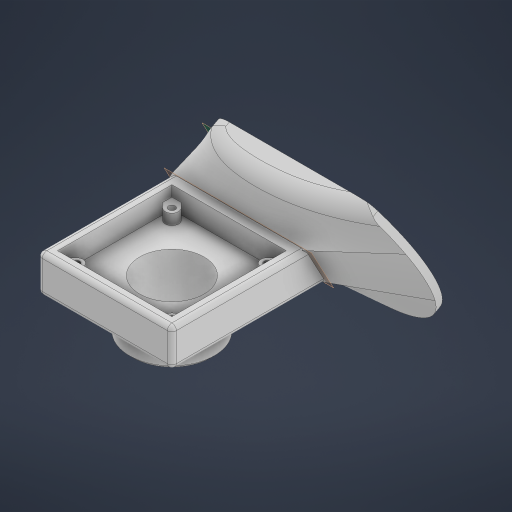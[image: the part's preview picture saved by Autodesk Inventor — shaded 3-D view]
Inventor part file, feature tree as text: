
AUTODESK INVENTOR PART (.ipt)
format: ipt  version: 2023 (Build 270158000, 158)  size: 587,264 bytes
history: native  units: in
note: dims shown in document units (in); Inventor stores cm internally (conversion verified against a paired STEP export)
features: sketch x10, extrude x7, hole x3, fillet x3, plane x2, chamfer x2, other x2, projected_geometry x2, loft x1
ambient origin geometry x8: Origin, YZ Plane, XZ Plane, XY Plane, X Axis, Y Axis, Z Axis, Center Point
bodies: Solid1 (feature_tree)
feature tree (32):
  extrude  "Extrusion1"  Depth=0.525in
  extrude  "Extrusion2"  Depth=0.4252in
  plane  "Work Plane1"
  extrude  "Extrusion3"  Depth=0.6in
  loft  "Loft1"
  extrude  "Extrusion4"  TaperAngle=0.0deg  [1 undecoded]
  hole  "Hole1"  [1 undecoded]
  extrude  "Extrusion5"  Depth=1.1875in
  extrude  "Extrusion6"  Depth=0.1839in
  hole  "Hole2"  [1 undecoded]
  plane  "Work Plane2"
  hole  "Hole3"  [1 undecoded]
  fillet  "Fillet1"  Radius=0.9792in
  chamfer  "Chamfer1"  Distance=0.4466in
  fillet  "Fillet2"  Radius=0.4in
  extrude  "Extrusion7"  Depth=0.15in
  fillet  "Fillet3"  Radius=0.0625in
  chamfer  "Chamfer2"  Distance=0.05in Angle=45.0deg
  sketch  "Sketch1"  dims[d0=1.875in d1=0.525in]
  sketch  "Sketch2"  dims[d2=1.875in d3=0.0in d4=0.4252in]
  sketch  "Sketch3"  dims[d5=1.875in d6=0.0in d7=0.6in]
  other  "Edges1"
  other  "Edges2"
  sketch  "Sketch4"  dims[d9=2.875in d10=0.1in d11=0.0in]
  projected_geometry  "Projected Loop1"
  sketch  "Sketch5"  dims[d12=0.0in d13=90.0deg d14=0.0in d15=90.0deg]
  sketch  "Sketch6"  dims[d16=1.6in d17=0.3in d18=0.0in]
  sketch  "Sketch7"  dims[d19=0.9in d20=0.75in d21=0.119in d22=0.25in d23=0.6871in d24=1.0in d25=0.8108in d26=1.1875in]
  projected_geometry  "Projected Loop2"
  sketch  "Sketch8"  dims[d27=0.5in d28=0.0in d29=0.1839in]
  sketch  "Sketch9"  dims[d30=1.3386in d31=0.15in d32=0.0in]
  sketch  "Sketch10"  dims[d33=0.094in d34=0.75in d35=0.251in d36=0.15in d37=0.6871in d38=1.0in d39=0.8108in d40=0.9792in d41=0.9792in d42=0.4466in d43=0.4in d44=0.65in d45=0.177in d46=0.75in d47=0.313in d48=0.45in d49=0.5635in d50=1.0in d51=0.8108in d52=0.0625in d53=0.05in d54=0.125in d55=45.0deg d56=0.0625in d57=1.0in d58=1.0in d59=0.0in d60=0.25in d61=0.02in d62=0.125in d63=45.0deg]
note: 4 required parameter values undecoded (feature->parameter linkage not recoverable at this tier; creation-order binding heuristic only, values carry confidence <= 0.55)
